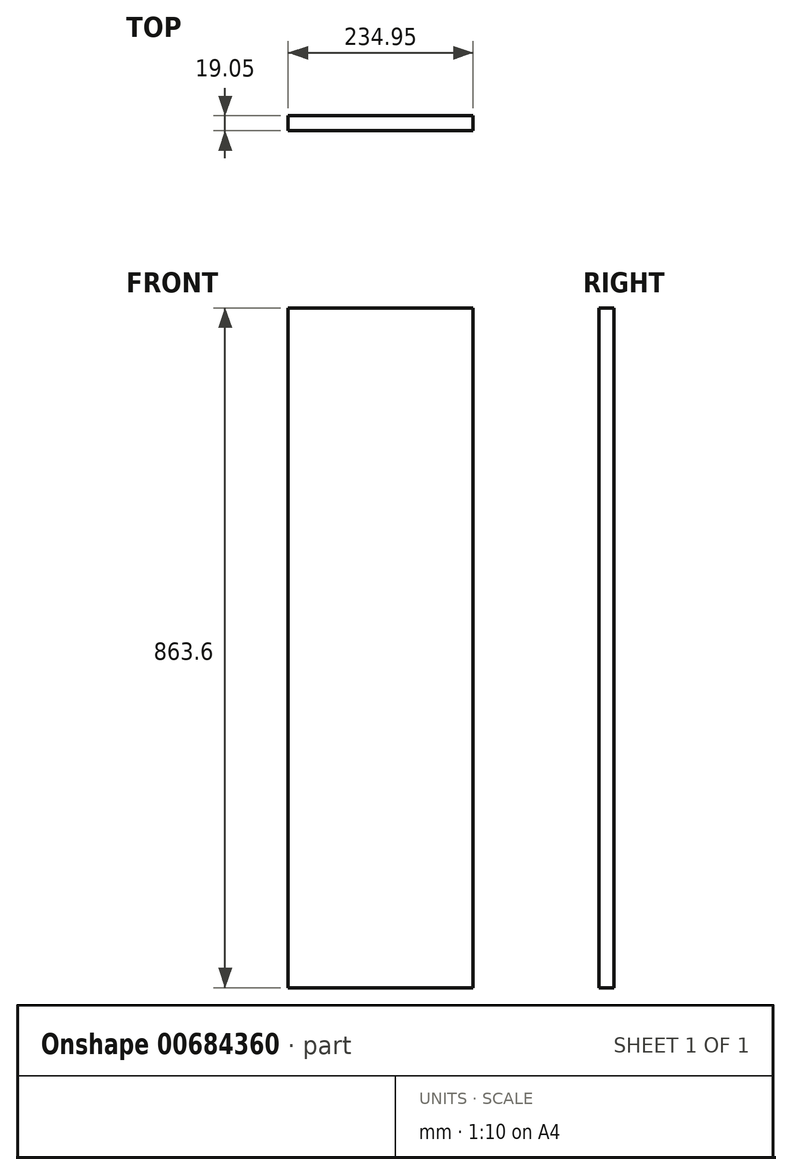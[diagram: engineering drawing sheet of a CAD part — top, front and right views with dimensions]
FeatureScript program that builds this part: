
annotation { "Feature Type Name" : "Feature", "Feature Type Description" : "" }
export const myFeature = defineFeature(function(context is Context, id is Id, definition is map)
    precondition{}
    {
        {
            var Q0;
            Q0=qCreatedBy(makeId("Front.planeOp"),FACE);
            var sketch = newSketch(context, id + "F0", { "sketchPlane" : qUnion([Q0])});
            skLineSegment(sketch, "E0.bottom", {"start": v(0, 0) * mm, "end": v(234.95, 0) * mm});
            skLineSegment(sketch, "E0.top", {"start": v(0, 863.6) * mm, "end": v(234.95, 863.6) * mm});
            skLineSegment(sketch, "E0.left", {"start": v(0, 0) * mm, "end": v(0, 863.6) * mm});
            skLineSegment(sketch, "E0.right", {"start": v(234.95, 0) * mm, "end": v(234.95, 863.6) * mm});
            skSolve(sketch);
        }
        {
            var Q0;
            Q0 = qSketchRegion(id + "F0", true);
            extrude(context, id + "F1", {"entities" : qUnion([Q0]), "depth" : 19.05 * mm, "offsetDistance" : 25.4 * mm});
        }
    });
